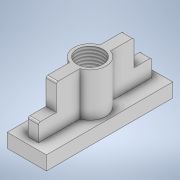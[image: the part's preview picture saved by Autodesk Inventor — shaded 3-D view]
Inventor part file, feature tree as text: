
AUTODESK INVENTOR PART (.ipt)
format: ipt  version: 2022 (Build 260153000, 153)  size: 152,576 bytes
history: native  units: mm
features: extrude x4, sketch x2, fillet x1, thread x1, projected_geometry x1
ambient origin geometry x8: Origin, YZ Plane, XZ Plane, XY Plane, X Axis, Y Axis, Z Axis, Center Point
bodies: Solid1 (feature_tree)
feature tree (9):
  sketch  "Sketch1"  dims[d0=4.5mm d2=3.0mm]
  extrude  "Extrusion1"  Depth=3.0mm
  extrude  "Extrusion2"  Depth=1.6mm TaperAngle=0.0deg
  extrude  "Extrusion3"  Depth=2.0mm TaperAngle=0.0deg
  fillet  "Fillet1"  Radius=5.0mm
  thread  "Thread1"  [1 undecoded]
  extrude  "Extrusion4"  Depth=10.0mm TaperAngle=0.0deg
  sketch  "Sketch2"  dims[d9=3.7mm d10=1.6mm d11=0.0mm d12=2.0mm d13=0.0mm d14=5.0mm d15=0.0mm d16=0.2mm d22=8.5mm d23=0.0mm d32=7.25mm d33=7.25mm d34=10.0mm d35=0.0mm]
  projected_geometry  "Projected Loop1"
note: 1 required parameter value undecoded (feature->parameter linkage not recoverable at this tier; creation-order binding heuristic only, values carry confidence <= 0.55)
